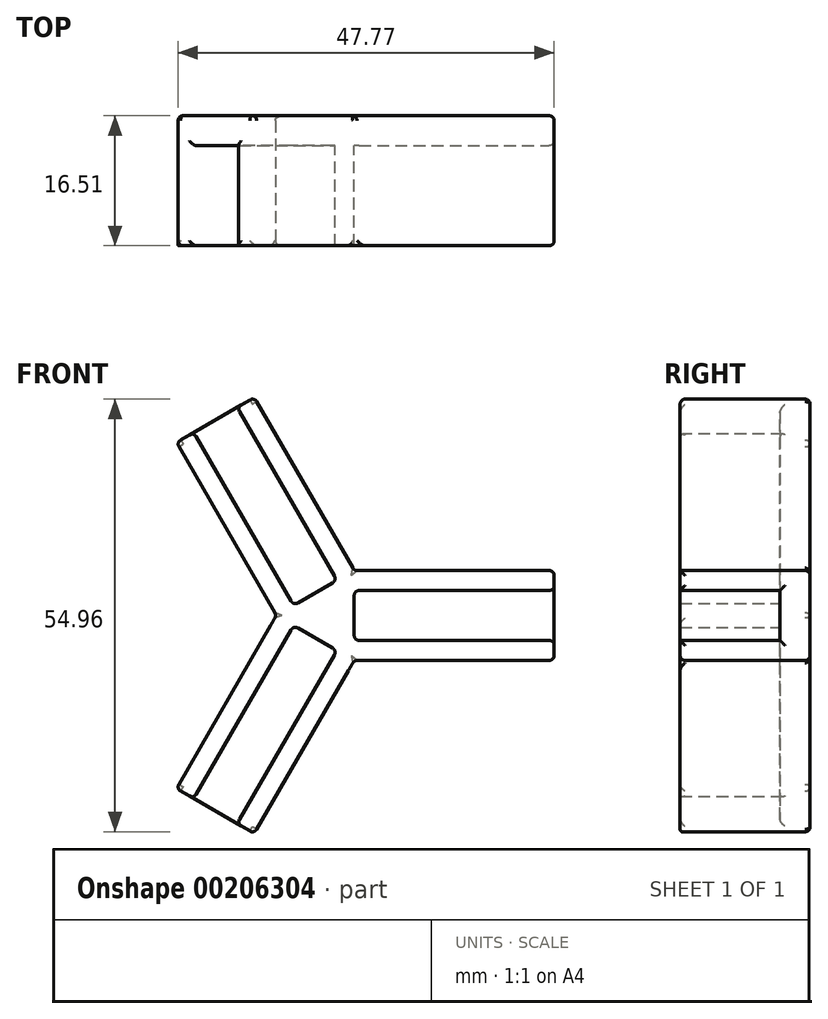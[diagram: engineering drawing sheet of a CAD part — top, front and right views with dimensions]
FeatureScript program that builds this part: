
annotation { "Feature Type Name" : "Feature", "Feature Type Description" : "" }
export const myFeature = defineFeature(function(context is Context, id is Id, definition is map)
    precondition{}
    {
        {
            var Q0;
            Q0=qCreatedBy(makeId("Front.planeOp"),FACE);
            var sketch = newSketch(context, id + "F0", { "sketchPlane" : qUnion([Q0])});
            skLineSegment(sketch, "E0", {"start": v(3.8, -5.72) * mm, "end": v(29.21, -5.72) * mm});
            skLineSegment(sketch, "E1", {"start": v(29.21, -5.72) * mm, "end": v(29.21, 5.72) * mm});
            skLineSegment(sketch, "E2", {"start": v(29.21, 5.71) * mm, "end": v(3.8, 5.71) * mm});
            skLineSegment(sketch, "E3", {"start": v(3.8, 5.71) * mm, "end": v(3.8, -5.72) * mm, "construction": true});
            skPoint(sketch, "E4", {"position": v(3.81, 0) * mm});
            skLineSegment(sketch, "E5.1.0", {"start": v(-8.9, 27.71) * mm, "end": v(-18.79, 22) * mm});
            skLineSegment(sketch, "E5.1.1", {"start": v(3.81, 5.71) * mm, "end": v(-8.9, 27.71) * mm});
            skLineSegment(sketch, "E5.1.2", {"start": v(-18.79, 22) * mm, "end": v(-6.09, 0) * mm});
            skPoint(sketch, "E5.1.3", {"position": v(-1.14, 2.86) * mm});
            skLineSegment(sketch, "E5.1.4", {"start": v(-6.09, 0) * mm, "end": v(3.8, 5.72) * mm, "construction": true});
            skLineSegment(sketch, "E5.2.0", {"start": v(-18.79, -22) * mm, "end": v(-8.9, -27.71) * mm});
            skLineSegment(sketch, "E5.2.1", {"start": v(-6.09, 0) * mm, "end": v(-18.79, -22) * mm});
            skLineSegment(sketch, "E5.2.2", {"start": v(-8.89, -27.71) * mm, "end": v(3.81, -5.72) * mm});
            skPoint(sketch, "E5.2.3", {"position": v(-1.14, -2.86) * mm});
            skLineSegment(sketch, "E5.2.4", {"start": v(3.81, -5.72) * mm, "end": v(-6.09, 0) * mm, "construction": true});
            skPoint(sketch, "E5.center", {"position": v(0.51, 0) * mm});
            skSolve(sketch);
        }
        {
            var Q0;
            Q0=makeQuery(id+"F0.imprint","IMPRINT",FACE,{"disambiguationData":[TD([[makeQuery(id+"F0.imprint","IMPRINT",EDGE,{"derivedFrom":sQuery(id+"F0.wireOp",EDGE,"E0")}),1.0]])]});
            extrude(context, id + "F1", {"entities" : qUnion([Q0]), "depth" : 3.8 * mm});
        }
        {
            var Q0;
            Q0=makeQuery(id+"F1.opExtrude","CAP_FACE",FACE,{"disambiguationData":[OSD([sQuery(id+"F0.wireOp",EDGE,"E0"),sQuery(id+"F0.wireOp",EDGE,"E1"),sQuery(id+"F0.wireOp",EDGE,"E2"),sQuery(id+"F0.wireOp",EDGE,"E5.1.0"),sQuery(id+"F0.wireOp",EDGE,"E5.1.1"),sQuery(id+"F0.wireOp",EDGE,"E5.1.2"),sQuery(id+"F0.wireOp",EDGE,"E5.2.0"),sQuery(id+"F0.wireOp",EDGE,"E5.2.1"),sQuery(id+"F0.wireOp",EDGE,"E5.2.2")])],"isStart":false});
            var sketch = newSketch(context, id + "F2", { "sketchPlane" : qUnion([Q0])});
            skLineSegment(sketch, "E6.1", {"start": v(29.21, 3.17) * mm, "end": v(4.45, 3.17) * mm});
            skLineSegment(sketch, "E6.4", {"start": v(4.44, -3.18) * mm, "end": v(29.21, -3.17) * mm});
            skLineSegment(sketch, "E7", {"start": v(-8.9, 27.71) * mm, "end": v(3.81, 5.71) * mm});
            skLineSegment(sketch, "E8", {"start": v(3.81, 5.71) * mm, "end": v(29.21, 5.71) * mm});
            skLineSegment(sketch, "E9", {"start": v(29.21, -5.72) * mm, "end": v(3.81, -5.72) * mm});
            skLineSegment(sketch, "E10", {"start": v(3.81, -5.72) * mm, "end": v(-8.89, -27.71) * mm});
            skLineSegment(sketch, "E11", {"start": v(-18.79, -22) * mm, "end": v(-6.09, 0) * mm});
            skLineSegment(sketch, "E12", {"start": v(-6.09, 0) * mm, "end": v(-18.79, 22) * mm});
            skLineSegment(sketch, "E13", {"start": v(29.21, 3.17) * mm, "end": v(29.21, 5.71) * mm});
            skLineSegment(sketch, "E14", {"start": v(29.21, -5.72) * mm, "end": v(29.21, -3.17) * mm});
            skLineSegment(sketch, "E15", {"start": v(-16.59, -23.27) * mm, "end": v(-18.79, -22) * mm});
            skLineSegment(sketch, "E16", {"start": v(-8.89, -27.71) * mm, "end": v(-11.09, -26.44) * mm});
            skLineSegment(sketch, "E17", {"start": v(-16.59, 23.27) * mm, "end": v(-18.79, 22) * mm});
            skLineSegment(sketch, "E18", {"start": v(3.81, 2.54) * mm, "end": v(3.8, -2.54) * mm});
            skPoint(sketch, "E19.visualSharp", {"position": v(2.34, 3.17) * mm});
            skArc(sketch, "E19.filletArc", {"start": v(4.45, 3.17) * mm, "mid": v(4, 2.99) * mm, "end": v(3.81, 2.54) * mm});
            skPoint(sketch, "E20.visualSharp", {"position": v(-3.16, 0) * mm});
            skPoint(sketch, "E21.visualSharp", {"position": v(2.34, -3.18) * mm});
            skArc(sketch, "E22.filletArc", {"start": v(3.8, -2.54) * mm, "mid": v(4, -2.99) * mm, "end": v(4.44, -3.18) * mm});
            skLineSegment(sketch, "E23.1.0", {"start": v(1.3, 5) * mm, "end": v(-11.09, 26.44) * mm});
            skLineSegment(sketch, "E23.1.1", {"start": v(-3.34, 1.59) * mm, "end": v(1.06, 4.13) * mm});
            skLineSegment(sketch, "E23.1.2", {"start": v(-16.59, 23.27) * mm, "end": v(-4.2, 1.82) * mm});
            skArc(sketch, "E23.1.3", {"start": v(-4.2, 1.82) * mm, "mid": v(-3.82, 1.52) * mm, "end": v(-3.34, 1.59) * mm});
            skArc(sketch, "E23.1.4", {"start": v(1.06, 4.13) * mm, "mid": v(1.36, 4.51) * mm, "end": v(1.3, 5) * mm});
            skLineSegment(sketch, "E23.2.0", {"start": v(-4.2, -1.82) * mm, "end": v(-16.59, -23.27) * mm});
            skLineSegment(sketch, "E23.2.1", {"start": v(1.06, -4.13) * mm, "end": v(-3.34, -1.59) * mm});
            skLineSegment(sketch, "E23.2.2", {"start": v(-11.09, -26.44) * mm, "end": v(1.3, -5) * mm});
            skArc(sketch, "E23.2.3", {"start": v(1.3, -5) * mm, "mid": v(1.36, -4.51) * mm, "end": v(1.06, -4.13) * mm});
            skArc(sketch, "E23.2.4", {"start": v(-3.34, -1.59) * mm, "mid": v(-3.82, -1.52) * mm, "end": v(-4.2, -1.82) * mm});
            skPoint(sketch, "E23.center", {"position": v(0.51, 0) * mm});
            skLineSegment(sketch, "E24", {"start": v(-11.09, 26.44) * mm, "end": v(-8.9, 27.71) * mm});
            skSolve(sketch);
        }
        {
            var Q0;
            Q0=makeQuery(id+"F2.imprint","IMPRINT",FACE,{"disambiguationData":[TD([[makeQuery(id+"F2.imprint","IMPRINT",EDGE,{"derivedFrom":sQuery(id+"F2.wireOp",EDGE,"E6.0")}),-1.0]])]});
            var Q1;
            Q1=makeQuery(id+"F2.imprint","IMPRINT",FACE,{"disambiguationData":[TD([[makeQuery(id+"F2.imprint","IMPRINT",EDGE,{"derivedFrom":sQuery(id+"F2.wireOp",EDGE,"E6.5")}),-1.0]])]});
            var Q2;
            Q2=makeQuery(id+"F2.imprint","IMPRINT",FACE,{"disambiguationData":[TD([[makeQuery(id+"F2.imprint","IMPRINT",EDGE,{"derivedFrom":sQuery(id+"F2.wireOp",EDGE,"E6.4")}),-1.0]])]});
            extrude(context, id + "F3", {"entities" : qUnion([Q0, Q1, Q2]), "operationType" : NewBodyOperationType.ADD, "depth" : 12.7 * mm});
        }
        {
            var Q0;
            Q0=makeQuery(id+"F1.opExtrude","CAP_EDGE",EDGE,{"disambiguationData":[OSD([sQuery(id+"F0.wireOp",EDGE,"E1")])],"isStart":true});
            var Q1;
            Q1=makeQuery(id+"F1.opExtrude","CAP_EDGE",EDGE,{"disambiguationData":[OSD([sQuery(id+"F0.wireOp",EDGE,"E2")])],"isStart":true});
            var Q2;
            Q2=makeQuery(id+"F1.opExtrude","CAP_EDGE",EDGE,{"disambiguationData":[OSD([sQuery(id+"F0.wireOp",EDGE,"E5.1.1")])],"isStart":true});
            var Q3;
            Q3=makeQuery(id+"F1.opExtrude","CAP_EDGE",EDGE,{"disambiguationData":[OSD([sQuery(id+"F0.wireOp",EDGE,"E5.1.0")])],"isStart":true});
            var Q4;
            Q4=makeQuery(id+"F1.opExtrude","CAP_EDGE",EDGE,{"disambiguationData":[OSD([sQuery(id+"F0.wireOp",EDGE,"E0")])],"isStart":true});
            var Q5;
            Q5=makeQuery(id+"F1.opExtrude","CAP_EDGE",EDGE,{"disambiguationData":[OSD([sQuery(id+"F0.wireOp",EDGE,"E5.2.2")])],"isStart":true});
            var Q6;
            Q6=makeQuery(id+"F1.opExtrude","CAP_EDGE",EDGE,{"disambiguationData":[OSD([sQuery(id+"F0.wireOp",EDGE,"E5.2.0")])],"isStart":true});
            var Q7;
            Q7=makeQuery(id+"F1.opExtrude","CAP_EDGE",EDGE,{"disambiguationData":[OSD([sQuery(id+"F0.wireOp",EDGE,"E5.1.2")])],"isStart":true});
            var Q8;
            Q8=makeQuery(id+"F1.opExtrude","CAP_EDGE",EDGE,{"disambiguationData":[OSD([sQuery(id+"F0.wireOp",EDGE,"E5.2.1")])],"isStart":true});
            fillet(context, id + "F4", {"entities" : qUnion([Q0, Q1, Q2, Q3, Q4, Q5, Q6, Q7, Q8]), "radius" : 0.64 * mm, "tangentPropagation" : true, "allowEdgeOverflow" : false});
        }
        {
            var Q0;
            Q0=makeQuery(id+"F3.boolean.opBoolean","MERGE",FACE,{"derivedFrom":[makeQuery(id+"F1.opExtrude","SWEPT_FACE",FACE,{"disambiguationData":[OSD([sQuery(id+"F0.wireOp",EDGE,"E5.1.1")])]}),makeQuery(id+"F3.opExtrude","SWEPT_FACE",FACE,{"disambiguationData":[OSD([sQuery(id+"F2.wireOp",EDGE,"E7")])]})]});
            var Q1;
            Q1=makeQuery(id+"F3.boolean.opBoolean","MERGE",FACE,{"derivedFrom":[makeQuery(id+"F1.opExtrude","SWEPT_FACE",FACE,{"disambiguationData":[OSD([sQuery(id+"F0.wireOp",EDGE,"E5.1.2")])]}),makeQuery(id+"F3.opExtrude","SWEPT_FACE",FACE,{"disambiguationData":[OSD([sQuery(id+"F2.wireOp",EDGE,"E12")])]})]});
            var Q2;
            Q2=makeQuery(id+"F3.boolean.opBoolean","MERGE",FACE,{"derivedFrom":[makeQuery(id+"F1.opExtrude","SWEPT_FACE",FACE,{"disambiguationData":[OSD([sQuery(id+"F0.wireOp",EDGE,"E5.1.0")])]}),makeQuery(id+"F3.opExtrude","SWEPT_FACE",FACE,{"disambiguationData":[OSD([sQuery(id+"F2.wireOp",EDGE,"E17")])]}),makeQuery(id+"F3.opExtrude","SWEPT_FACE",FACE,{"disambiguationData":[OSD([sQuery(id+"F2.wireOp",EDGE,"6rVtuYrV-5hmu-PjZr-s70o-oajAdRnHGXNe")])]})]});
            var Q3;
            Q3=makeQuery(id+"F3.boolean.opBoolean","MERGE",FACE,{"derivedFrom":[makeQuery(id+"F1.opExtrude","SWEPT_FACE",FACE,{"disambiguationData":[OSD([sQuery(id+"F0.wireOp",EDGE,"E1")])]}),makeQuery(id+"F3.opExtrude","SWEPT_FACE",FACE,{"disambiguationData":[OSD([sQuery(id+"F2.wireOp",EDGE,"E13")])]}),makeQuery(id+"F3.opExtrude","SWEPT_FACE",FACE,{"disambiguationData":[OSD([sQuery(id+"F2.wireOp",EDGE,"E14")])]})]});
            var Q4;
            Q4=makeQuery(id+"F3.boolean.opBoolean","MERGE",FACE,{"derivedFrom":[makeQuery(id+"F1.opExtrude","SWEPT_FACE",FACE,{"disambiguationData":[OSD([sQuery(id+"F0.wireOp",EDGE,"E0")])]}),makeQuery(id+"F3.opExtrude","SWEPT_FACE",FACE,{"disambiguationData":[OSD([sQuery(id+"F2.wireOp",EDGE,"E9")])]})]});
            var Q5;
            Q5=makeQuery(id+"F3.boolean.opBoolean","MERGE",FACE,{"derivedFrom":[makeQuery(id+"F1.opExtrude","SWEPT_FACE",FACE,{"disambiguationData":[OSD([sQuery(id+"F0.wireOp",EDGE,"E5.2.0")])]}),makeQuery(id+"F3.opExtrude","SWEPT_FACE",FACE,{"disambiguationData":[OSD([sQuery(id+"F2.wireOp",EDGE,"E15")])]}),makeQuery(id+"F3.opExtrude","SWEPT_FACE",FACE,{"disambiguationData":[OSD([sQuery(id+"F2.wireOp",EDGE,"E16")])]})]});
            fillet(context, id + "F5", {"entities" : qUnion([Q0, Q1, Q2, Q3, Q4, Q5]), "radius" : 0.64 * mm, "tangentPropagation" : true, "allowEdgeOverflow" : false});
        }
    });
